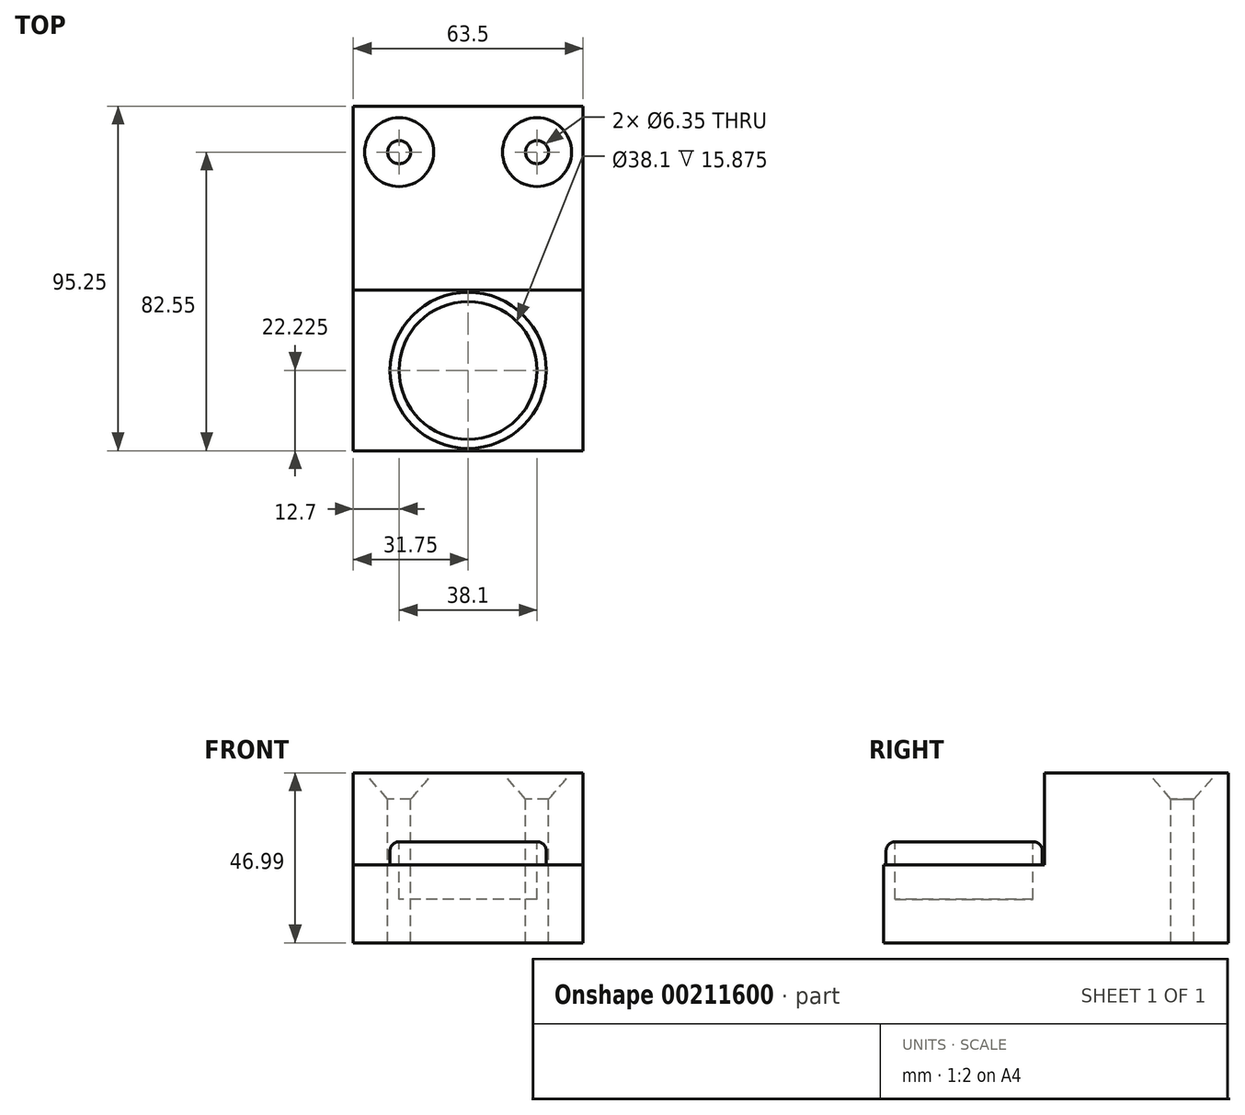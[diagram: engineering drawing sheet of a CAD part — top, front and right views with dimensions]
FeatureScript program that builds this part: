
annotation { "Feature Type Name" : "Feature", "Feature Type Description" : "" }
export const myFeature = defineFeature(function(context is Context, id is Id, definition is map)
    precondition{}
    {
        {
            var Q0;
            Q0=qCreatedBy(makeId("Right.planeOp"),FACE);
            var sketch = newSketch(context, id + "F0", { "sketchPlane" : qUnion([Q0])});
            skLineSegment(sketch, "E0", {"start": v(0, 0) * mm, "end": v(95.25, 0) * mm});
            skLineSegment(sketch, "E1", {"start": v(95.25, 0) * mm, "end": v(95.25, 47) * mm});
            skLineSegment(sketch, "E2", {"start": v(95.25, 47) * mm, "end": v(44.45, 46.99) * mm});
            skLineSegment(sketch, "E3", {"start": v(44.45, 47) * mm, "end": v(44.45, 21.59) * mm});
            skLineSegment(sketch, "E4", {"start": v(44.45, 21.59) * mm, "end": v(0, 21.59) * mm});
            skLineSegment(sketch, "E5", {"start": v(0, 21.59) * mm, "end": v(0, 0) * mm});
            skSolve(sketch);
        }
        {
            var Q0;
            Q0=makeQuery(id+"F0.imprint","IMPRINT",FACE,{"disambiguationData":[TD([[makeQuery(id+"F0.imprint","IMPRINT",EDGE,{"derivedFrom":sQuery(id+"F0.wireOp",EDGE,"E0")}),1.0]])]});
            extrude(context, id + "F1", {"entities" : qUnion([Q0]), "oppositeDirection" : true, "depth" : 63.5 * mm});
        }
        {
            var Q0;
            Q0=makeQuery(id+"F1.opExtrude","SWEPT_FACE",FACE,{"disambiguationData":[OSD([sQuery(id+"F0.wireOp",EDGE,"E4")])]});
            var sketch = newSketch(context, id + "F2", { "sketchPlane" : qUnion([Q0])});
            skLineSegment(sketch, "E6", {"start": v(-63.5, 44.45) * mm, "end": v(0, 0) * mm, "construction": true});
            skLineSegment(sketch, "E7", {"start": v(-63.5, 0) * mm, "end": v(0, 44.45) * mm, "construction": true});
            skCircle(sketch, "E8", {"center": v(-31.75, 22.23) * mm, "radius": 19.05 * mm});
            skSolve(sketch);
        }
        {
            var Q0;
            Q0=makeQuery(id+"F2.imprint","IMPRINT",FACE,{"disambiguationData":[TD([[makeQuery(id+"F2.imprint","IMPRINT",EDGE,{"derivedFrom":sQuery(id+"F2.wireOp",EDGE,"E8")}),1.0]])]});
            extrude(context, id + "F3", {"entities" : qUnion([Q0]), "operationType" : NewBodyOperationType.REMOVE, "oppositeDirection" : true, "depth" : 9.52 * mm});
        }
        {
            var Q0;
            Q0=makeQuery(id+"F1.opExtrude","SWEPT_FACE",FACE,{"disambiguationData":[OSD([sQuery(id+"F0.wireOp",EDGE,"E4")])]});
            var sketch = newSketch(context, id + "F4", { "sketchPlane" : qUnion([Q0])});
            skCircle(sketch, "E9", {"center": v(-31.75, 22.23) * mm, "radius": 19.05 * mm});
            skCircle(sketch, "E10", {"center": v(-31.75, 22.23) * mm, "radius": 21.59 * mm});
            skSolve(sketch);
        }
        {
            var Q0;
            Q0=makeQuery(id+"F4.imprint","IMPRINT",FACE,{"disambiguationData":[TD([[makeQuery(id+"F4.imprint","IMPRINT",EDGE,{"derivedFrom":sQuery(id+"F4.wireOp",EDGE,"E9")}),-1.0]])]});
            extrude(context, id + "F5", {"entities" : qUnion([Q0]), "operationType" : NewBodyOperationType.ADD, "depth" : 6.35 * mm});
        }
        {
            var Q0;
            Q0=makeQuery(id+"F5.opExtrude","CAP_EDGE",EDGE,{"disambiguationData":[OSD([sQuery(id+"F4.wireOp",EDGE,"E10")])],"isStart":false});
            fillet(context, id + "F6", {"entities" : qUnion([Q0]), "radius" : 2.54 * mm, "tangentPropagation" : true, "allowEdgeOverflow" : false});
        }
        {
            var Q0;
            Q0=makeQuery(id+"F1.opExtrude","SWEPT_FACE",FACE,{"disambiguationData":[OSD([sQuery(id+"F0.wireOp",EDGE,"E2")])]});
            var sketch = newSketch(context, id + "F7", { "sketchPlane" : qUnion([Q0])});
            skLineSegment(sketch, "E11", {"start": v(-63.5, 82.55) * mm, "end": v(0, 82.55) * mm, "construction": true});
            skPoint(sketch, "E12", {"position": v(-50.8, 82.55) * mm});
            skPoint(sketch, "E13", {"position": v(-12.7, 82.55) * mm});
            skSolve(sketch);
        }
        {
            var Q0;
            Q0=sQuery(id+"F7.wireOp",VERTEX,"E12");
            var Q1;
            Q1=sQuery(id+"F7.wireOp",VERTEX,"E13");
            var Q2;
            Q2=makeQuery(id+"F1.opExtrude","SWEPT_BODY",BODY,{"disambiguationData":[OSD([sQuery(id+"F0.wireOp",EDGE,"E0"),sQuery(id+"F0.wireOp",EDGE,"E1"),sQuery(id+"F0.wireOp",EDGE,"E2"),sQuery(id+"F0.wireOp",EDGE,"E3"),sQuery(id+"F0.wireOp",EDGE,"E4"),sQuery(id+"F0.wireOp",EDGE,"E5")])]});
            hole(context, id + "F8", {"style" : HoleStyle.C_SINK, "endStyle" : HoleEndStyle.THROUGH, "holeDiameter" : 6.35 * mm, "cSinkDiameter" : 19.05 * mm, "cSinkAngle" : 82 * degree, "startFromSketch" : true, "locations" : qUnion([Q0, Q1]), "scope" : qUnion([Q2]), "isTappedThrough" : true});
        }
    });
